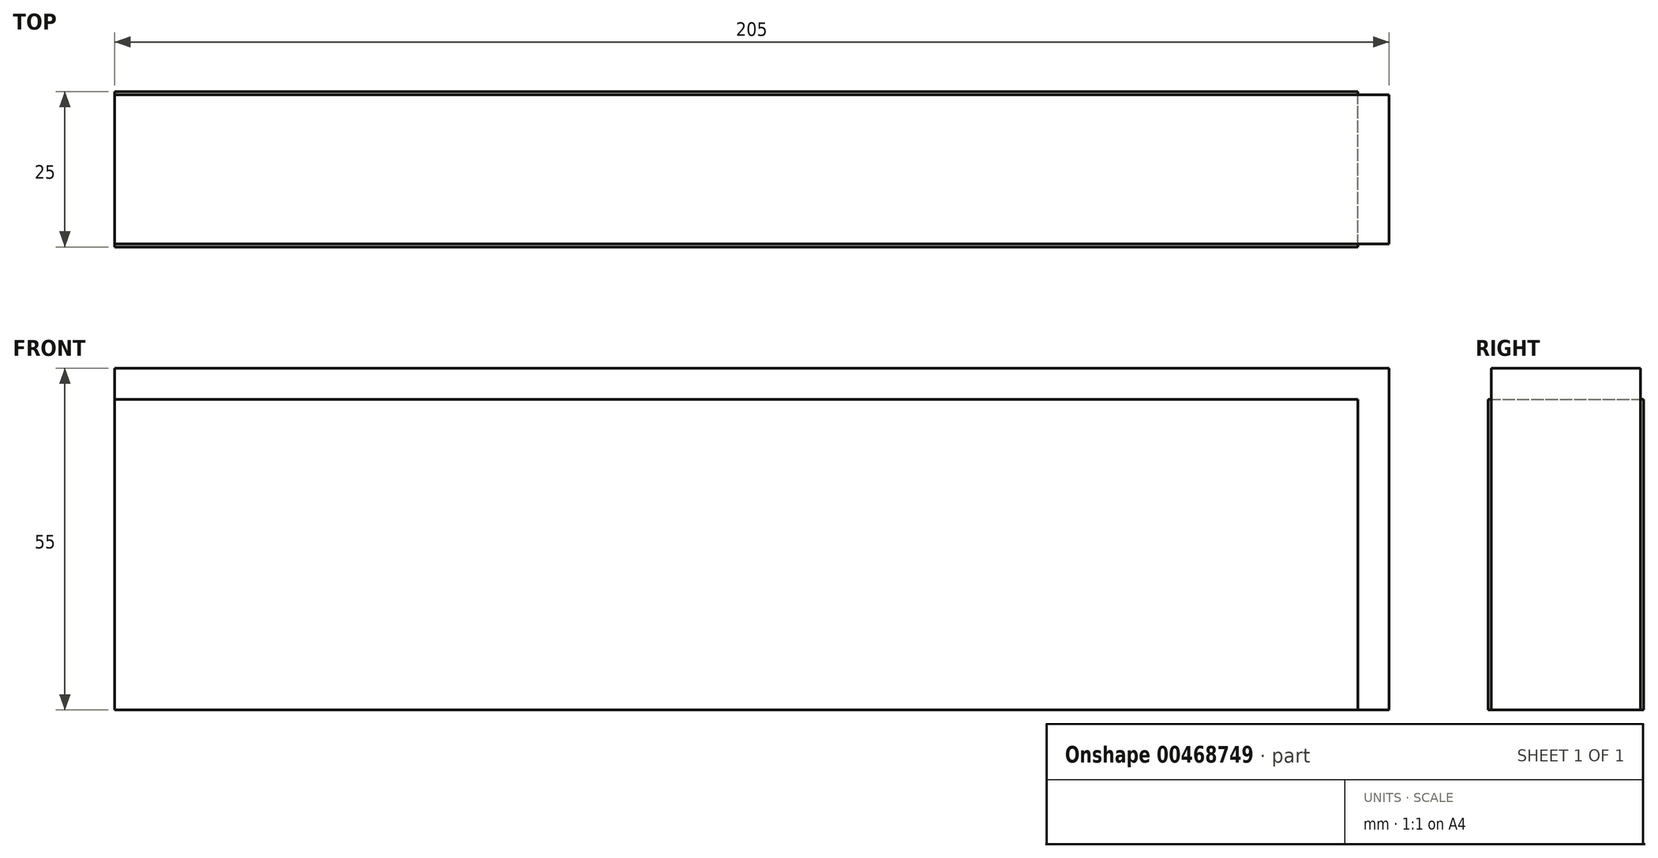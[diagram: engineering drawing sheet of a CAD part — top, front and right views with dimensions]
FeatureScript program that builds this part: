
annotation { "Feature Type Name" : "Feature", "Feature Type Description" : "" }
export const myFeature = defineFeature(function(context is Context, id is Id, definition is map)
    precondition{}
    {
        {
            var Q0;
            Q0=qCreatedBy(makeId("Front.planeOp"),FACE);
            var sketch = newSketch(context, id + "F0", { "sketchPlane" : qUnion([Q0])});
            skLineSegment(sketch, "E0.bottom", {"start": v(100, 25) * mm, "end": v(-100, 25) * mm});
            skLineSegment(sketch, "E0.top", {"start": v(100, -25) * mm, "end": v(-100, -25) * mm});
            skLineSegment(sketch, "E0.left", {"start": v(100, 25) * mm, "end": v(100, -25) * mm});
            skLineSegment(sketch, "E0.right", {"start": v(-100, 25) * mm, "end": v(-100, -25) * mm});
            skPoint(sketch, "E0.middle", {"position": v(0, 0) * mm});
            skSolve(sketch);
        }
        {
            var Q0;
            Q0=qSketchRegion(id+"F0",true);
            extrude(context, id + "F1", {"entities" : qUnion([Q0]), "endBound" : BoundingType.SYMMETRIC, "depth" : 25 * mm});
        }
        {
            var Q0;
            Q0=qCreatedBy(makeId("Front.planeOp"),FACE);
            var sketch = newSketch(context, id + "F2", { "sketchPlane" : qUnion([Q0])});
            skLineSegment(sketch, "E1.0.0", {"start": v(-100, -25) * mm, "end": v(100, -25) * mm, "construction": true});
            skLineSegment(sketch, "E1.0.1", {"start": v(100, -25) * mm, "end": v(100, 25) * mm, "construction": true});
            skLineSegment(sketch, "E1.0.2", {"start": v(100, 25) * mm, "end": v(-100, 25) * mm, "construction": true});
            skLineSegment(sketch, "E1.0.3", {"start": v(-100, 25) * mm, "end": v(-100, -25) * mm, "construction": true});
            skLineSegment(sketch, "E2.bottom", {"start": v(-100, -25) * mm, "end": v(105, -25) * mm});
            skLineSegment(sketch, "E2.top", {"start": v(-100, 30) * mm, "end": v(105, 30) * mm});
            skLineSegment(sketch, "E2.left", {"start": v(-100, -25) * mm, "end": v(-100, 30) * mm});
            skLineSegment(sketch, "E2.right", {"start": v(105, -25) * mm, "end": v(105, 30) * mm});
            skSolve(sketch);
        }
        {
            var Q0;
            Q0=qSketchRegion(id+"F2",true);
            extrude(context, id + "F3", {"entities" : qUnion([Q0]), "endBound" : BoundingType.SYMMETRIC, "depth" : 24 * mm});
        }
    });
